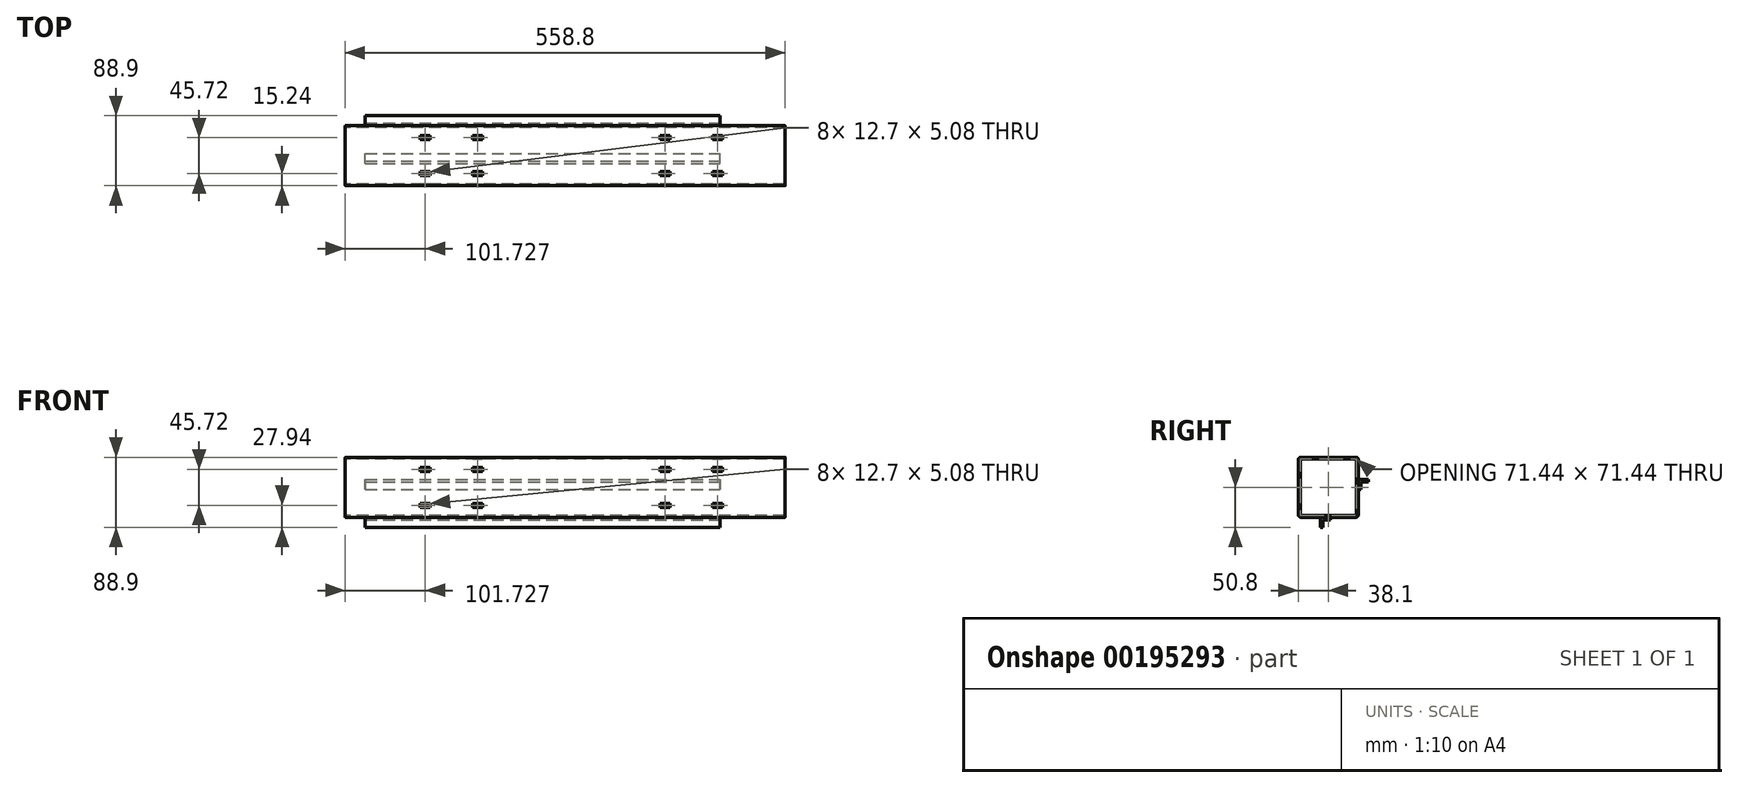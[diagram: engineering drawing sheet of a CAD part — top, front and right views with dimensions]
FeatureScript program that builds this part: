
annotation { "Feature Type Name" : "Feature", "Feature Type Description" : "" }
export const myFeature = defineFeature(function(context is Context, id is Id, definition is map)
    precondition{}
    {
        {
            var Q0;
            Q0=qCreatedBy(makeId("Right.planeOp"),FACE);
            var sketch = newSketch(context, id + "F0", { "sketchPlane" : qUnion([Q0])});
            skLineSegment(sketch, "E0.bottom", {"start": v(3.05, 0) * mm, "end": v(73.15, 0) * mm});
            skLineSegment(sketch, "E0.top", {"start": v(3.05, -76.2) * mm, "end": v(73.15, -76.2) * mm});
            skLineSegment(sketch, "E0.left", {"start": v(0, -3.05) * mm, "end": v(0, -73.15) * mm});
            skLineSegment(sketch, "E0.right", {"start": v(76.2, -3.05) * mm, "end": v(76.2, -73.15) * mm});
            skPoint(sketch, "E1.visualSharp", {"position": v(76.2, -76.2) * mm});
            skArc(sketch, "E1.filletArc", {"start": v(73.15, -76.2) * mm, "mid": v(75.3, -75.3) * mm, "end": v(76.2, -73.15) * mm});
            skPoint(sketch, "E2.visualSharp", {"position": v(76.2, 0) * mm});
            skArc(sketch, "E2.filletArc", {"start": v(76.2, -3.05) * mm, "mid": v(75.3, -0.9) * mm, "end": v(73.15, 0) * mm});
            skPoint(sketch, "E3.visualSharp", {"position": v(0, 0) * mm});
            skArc(sketch, "E3.filletArc", {"start": v(3.05, 0) * mm, "mid": v(0.9, -0.9) * mm, "end": v(0, -3.05) * mm});
            skPoint(sketch, "E4.visualSharp", {"position": v(0, -76.2) * mm});
            skArc(sketch, "E4.filletArc", {"start": v(0, -73.15) * mm, "mid": v(0.9, -75.3) * mm, "end": v(3.05, -76.2) * mm});
            skArc(sketch, "E5.0", {"start": v(73.82, -3.05) * mm, "mid": v(73.62, -2.58) * mm, "end": v(73.15, -2.38) * mm});
            skLineSegment(sketch, "E5.1", {"start": v(3.05, -2.38) * mm, "end": v(73.15, -2.38) * mm});
            skLineSegment(sketch, "E5.2", {"start": v(73.82, -3.05) * mm, "end": v(73.82, -73.15) * mm});
            skArc(sketch, "E5.3", {"start": v(3.05, -2.38) * mm, "mid": v(2.58, -2.58) * mm, "end": v(2.38, -3.05) * mm});
            skArc(sketch, "E5.4", {"start": v(73.15, -73.82) * mm, "mid": v(73.62, -73.62) * mm, "end": v(73.82, -73.15) * mm});
            skLineSegment(sketch, "E5.5", {"start": v(3.05, -73.82) * mm, "end": v(73.15, -73.82) * mm});
            skArc(sketch, "E5.6", {"start": v(2.38, -73.15) * mm, "mid": v(2.58, -73.62) * mm, "end": v(3.05, -73.82) * mm});
            skLineSegment(sketch, "E5.7", {"start": v(2.38, -3.05) * mm, "end": v(2.38, -73.15) * mm});
            skSolve(sketch);
        }
        {
            var Q0;
            Q0=makeQuery(id+"F0.imprint","IMPRINT",FACE,{"disambiguationData":[TD([[makeQuery(id+"F0.imprint","IMPRINT",EDGE,{"derivedFrom":sQuery(id+"F0.wireOp",EDGE,"E0.bottom")}),-1.0]])]});
            extrude(context, id + "F1", {"entities" : qUnion([Q0]), "depth" : 558.8 * mm});
        }
        {
            var Q0;
            Q0=makeQuery(id+"F1.opExtrude","SWEPT_FACE",FACE,{"disambiguationData":[OSD([sQuery(id+"F0.wireOp",EDGE,"E0.bottom")])]});
            var sketch = newSketch(context, id + "F2", { "sketchPlane" : qUnion([Q0])});
            skLineSegment(sketch, "E6", {"start": v(466.73, 76.2) * mm, "end": v(466.73, 0) * mm, "construction": true});
            skLineSegment(sketch, "E7", {"start": v(412.88, 76.2) * mm, "end": v(412.88, 0) * mm, "construction": true});
            skLineSegment(sketch, "E8.bottom", {"start": v(466.73, 63.5) * mm, "end": v(479.43, 63.5) * mm});
            skLineSegment(sketch, "E8.top", {"start": v(466.73, 58.42) * mm, "end": v(479.43, 58.42) * mm});
            skLineSegment(sketch, "E8.left", {"start": v(466.73, 63.5) * mm, "end": v(466.73, 58.42) * mm});
            skLineSegment(sketch, "E8.right", {"start": v(479.43, 63.5) * mm, "end": v(479.43, 58.42) * mm});
            skLineSegment(sketch, "E9.bottom", {"start": v(466.73, 17.78) * mm, "end": v(479.43, 17.78) * mm});
            skLineSegment(sketch, "E9.top", {"start": v(466.73, 12.7) * mm, "end": v(479.43, 12.7) * mm});
            skLineSegment(sketch, "E9.left", {"start": v(466.73, 17.78) * mm, "end": v(466.73, 12.7) * mm});
            skLineSegment(sketch, "E9.right", {"start": v(479.43, 17.78) * mm, "end": v(479.43, 12.7) * mm});
            skLineSegment(sketch, "E10.bottom", {"start": v(412.88, 58.42) * mm, "end": v(400.18, 58.42) * mm});
            skLineSegment(sketch, "E10.top", {"start": v(412.88, 63.5) * mm, "end": v(400.18, 63.5) * mm});
            skLineSegment(sketch, "E10.left", {"start": v(412.88, 58.42) * mm, "end": v(412.88, 63.5) * mm});
            skLineSegment(sketch, "E10.right", {"start": v(400.18, 58.42) * mm, "end": v(400.18, 63.5) * mm});
            skLineSegment(sketch, "E11.bottom", {"start": v(412.88, 17.78) * mm, "end": v(400.18, 17.78) * mm});
            skLineSegment(sketch, "E11.top", {"start": v(412.88, 12.7) * mm, "end": v(400.18, 12.7) * mm});
            skLineSegment(sketch, "E11.left", {"start": v(412.88, 17.78) * mm, "end": v(412.88, 12.7) * mm});
            skLineSegment(sketch, "E11.right", {"start": v(400.18, 17.78) * mm, "end": v(400.18, 12.7) * mm});
            skPoint(sketch, "E12", {"position": v(466.73, 38.1) * mm});
            skPoint(sketch, "E13", {"position": v(412.88, 38.1) * mm});
            skLineSegment(sketch, "E14", {"start": v(161.93, 73.15) * mm, "end": v(161.93, 3.05) * mm, "construction": true});
            skLineSegment(sketch, "E15.bottom", {"start": v(161.93, 63.5) * mm, "end": v(174.63, 63.5) * mm});
            skLineSegment(sketch, "E15.top", {"start": v(161.93, 58.42) * mm, "end": v(174.63, 58.42) * mm});
            skLineSegment(sketch, "E15.left", {"start": v(161.93, 63.5) * mm, "end": v(161.93, 58.42) * mm});
            skLineSegment(sketch, "E15.right", {"start": v(174.63, 63.5) * mm, "end": v(174.63, 58.42) * mm});
            skLineSegment(sketch, "E16.bottom", {"start": v(161.93, 17.78) * mm, "end": v(174.63, 17.78) * mm});
            skLineSegment(sketch, "E16.top", {"start": v(161.93, 12.7) * mm, "end": v(174.63, 12.7) * mm});
            skLineSegment(sketch, "E16.left", {"start": v(161.93, 17.78) * mm, "end": v(161.93, 12.7) * mm});
            skLineSegment(sketch, "E16.right", {"start": v(174.63, 17.78) * mm, "end": v(174.63, 12.7) * mm});
            skLineSegment(sketch, "E17.bottom", {"start": v(108.08, 58.42) * mm, "end": v(95.38, 58.42) * mm});
            skLineSegment(sketch, "E17.top", {"start": v(108.08, 63.5) * mm, "end": v(95.38, 63.5) * mm});
            skLineSegment(sketch, "E17.left", {"start": v(108.08, 58.42) * mm, "end": v(108.08, 63.5) * mm});
            skLineSegment(sketch, "E17.right", {"start": v(95.38, 58.42) * mm, "end": v(95.38, 63.5) * mm});
            skLineSegment(sketch, "E18.bottom", {"start": v(108.08, 17.78) * mm, "end": v(95.38, 17.78) * mm});
            skLineSegment(sketch, "E18.top", {"start": v(108.08, 12.7) * mm, "end": v(95.38, 12.7) * mm});
            skLineSegment(sketch, "E18.left", {"start": v(108.08, 17.78) * mm, "end": v(108.08, 12.7) * mm});
            skLineSegment(sketch, "E18.right", {"start": v(95.38, 17.78) * mm, "end": v(95.38, 12.7) * mm});
            skPoint(sketch, "E19", {"position": v(161.93, 38.1) * mm});
            skPoint(sketch, "E20", {"position": v(108.08, 38.1) * mm});
            skLineSegment(sketch, "E21", {"start": v(108.08, 73.15) * mm, "end": v(108.08, 3.05) * mm, "construction": true});
            skPoint(sketch, "E22", {"position": v(406.53, 38.1) * mm});
            skPoint(sketch, "E22.positionSnap0", {"position": v(406.53, 58.42) * mm});
            skPoint(sketch, "E23", {"position": v(473.08, 38.1) * mm});
            skPoint(sketch, "E23.positionSnap0", {"position": v(473.08, 58.42) * mm});
            skPoint(sketch, "E24", {"position": v(168.28, 38.1) * mm});
            skPoint(sketch, "E24.positionSnap0", {"position": v(168.28, 58.42) * mm});
            skPoint(sketch, "E25", {"position": v(101.73, 38.1) * mm});
            skPoint(sketch, "E25.positionSnap0", {"position": v(101.73, 58.42) * mm});
            skSolve(sketch);
        }
        {
            var Q0;
            Q0=makeQuery(id+"F2.imprint","IMPRINT",FACE,{"disambiguationData":[TD([[makeQuery(id+"F2.imprint","IMPRINT",EDGE,{"derivedFrom":sQuery(id+"F2.wireOp",EDGE,"E8.bottom")}),-1.0]])]});
            var Q1;
            Q1=makeQuery(id+"F2.imprint","IMPRINT",FACE,{"disambiguationData":[TD([[makeQuery(id+"F2.imprint","IMPRINT",EDGE,{"derivedFrom":sQuery(id+"F2.wireOp",EDGE,"E9.bottom")}),-1.0]])]});
            var Q2;
            Q2=makeQuery(id+"F2.imprint","IMPRINT",FACE,{"disambiguationData":[TD([[makeQuery(id+"F2.imprint","IMPRINT",EDGE,{"derivedFrom":sQuery(id+"F2.wireOp",EDGE,"E11.bottom")}),1.0]])]});
            var Q3;
            Q3=makeQuery(id+"F2.imprint","IMPRINT",FACE,{"disambiguationData":[TD([[makeQuery(id+"F2.imprint","IMPRINT",EDGE,{"derivedFrom":sQuery(id+"F2.wireOp",EDGE,"E10.bottom")}),-1.0]])]});
            extrude(context, id + "F3", {"entities" : qUnion([Q0, Q1, Q2, Q3]), "operationType" : NewBodyOperationType.REMOVE, "oppositeDirection" : true, "depth" : 2.38 * mm});
        }
        {
            var Q0;
            Q0=makeQuery(id+"F2.imprint","IMPRINT",FACE,{"disambiguationData":[TD([[makeQuery(id+"F2.imprint","IMPRINT",EDGE,{"derivedFrom":sQuery(id+"F2.wireOp",EDGE,"E15.bottom")}),-1.0]])]});
            var Q1;
            Q1=makeQuery(id+"F2.imprint","IMPRINT",FACE,{"disambiguationData":[TD([[makeQuery(id+"F2.imprint","IMPRINT",EDGE,{"derivedFrom":sQuery(id+"F2.wireOp",EDGE,"E16.bottom")}),-1.0]])]});
            var Q2;
            Q2=makeQuery(id+"F2.imprint","IMPRINT",FACE,{"disambiguationData":[TD([[makeQuery(id+"F2.imprint","IMPRINT",EDGE,{"derivedFrom":sQuery(id+"F2.wireOp",EDGE,"E18.bottom")}),1.0]])]});
            var Q3;
            Q3=makeQuery(id+"F2.imprint","IMPRINT",FACE,{"disambiguationData":[TD([[makeQuery(id+"F2.imprint","IMPRINT",EDGE,{"derivedFrom":sQuery(id+"F2.wireOp",EDGE,"E17.bottom")}),-1.0]])]});
            extrude(context, id + "F4", {"entities" : qUnion([Q0, Q1, Q2, Q3]), "operationType" : NewBodyOperationType.REMOVE, "oppositeDirection" : true, "depth" : 2.38 * mm});
        }
        {
            var Q0;
            Q0=makeQuery(id+"F1.opExtrude","SWEPT_FACE",FACE,{"disambiguationData":[OSD([sQuery(id+"F0.wireOp",EDGE,"E0.left")])]});
            var sketch = newSketch(context, id + "F5", { "sketchPlane" : qUnion([Q0])});
            skLineSegment(sketch, "E26", {"start": v(466.73, -3.05) * mm, "end": v(466.73, -73.15) * mm, "construction": true});
            skLineSegment(sketch, "E27", {"start": v(412.88, -3.05) * mm, "end": v(412.88, -73.15) * mm, "construction": true});
            skLineSegment(sketch, "E28", {"start": v(161.93, -3.05) * mm, "end": v(161.93, -73.15) * mm, "construction": true});
            skPoint(sketch, "E28.endSnap0", {"position": v(279.4, -73.15) * mm});
            skLineSegment(sketch, "E29", {"start": v(108.08, -3.05) * mm, "end": v(108.08, -73.15) * mm, "construction": true});
            skPoint(sketch, "E30", {"position": v(466.73, -38.1) * mm});
            skPoint(sketch, "E31", {"position": v(412.88, -38.1) * mm});
            skPoint(sketch, "E32", {"position": v(161.93, -38.1) * mm});
            skPoint(sketch, "E33", {"position": v(108.08, -38.1) * mm});
            skLineSegment(sketch, "E34.bottom", {"start": v(466.73, -12.7) * mm, "end": v(479.43, -12.7) * mm});
            skLineSegment(sketch, "E34.top", {"start": v(466.73, -17.78) * mm, "end": v(479.43, -17.78) * mm});
            skLineSegment(sketch, "E34.left", {"start": v(466.73, -12.7) * mm, "end": v(466.73, -17.78) * mm});
            skLineSegment(sketch, "E34.right", {"start": v(479.43, -12.7) * mm, "end": v(479.43, -17.78) * mm});
            skLineSegment(sketch, "E35.bottom", {"start": v(466.73, -58.42) * mm, "end": v(479.43, -58.42) * mm});
            skLineSegment(sketch, "E35.top", {"start": v(466.73, -63.5) * mm, "end": v(479.43, -63.5) * mm});
            skLineSegment(sketch, "E35.left", {"start": v(466.73, -58.42) * mm, "end": v(466.73, -63.5) * mm});
            skLineSegment(sketch, "E35.right", {"start": v(479.43, -58.42) * mm, "end": v(479.43, -63.5) * mm});
            skLineSegment(sketch, "E36.left", {"start": v(412.88, -58.42) * mm, "end": v(412.88, -63.5) * mm});
            skLineSegment(sketch, "E37.left", {"start": v(412.88, -12.7) * mm, "end": v(412.88, -17.78) * mm});
            skLineSegment(sketch, "E38.bottom", {"start": v(161.93, -12.7) * mm, "end": v(174.63, -12.7) * mm});
            skLineSegment(sketch, "E38.top", {"start": v(161.93, -17.78) * mm, "end": v(174.63, -17.78) * mm});
            skLineSegment(sketch, "E38.left", {"start": v(161.93, -12.7) * mm, "end": v(161.93, -17.78) * mm});
            skLineSegment(sketch, "E38.right", {"start": v(174.63, -12.7) * mm, "end": v(174.63, -17.78) * mm});
            skLineSegment(sketch, "E39.bottom", {"start": v(161.93, -58.42) * mm, "end": v(174.63, -58.42) * mm});
            skLineSegment(sketch, "E39.top", {"start": v(161.93, -63.5) * mm, "end": v(174.63, -63.5) * mm});
            skLineSegment(sketch, "E39.left", {"start": v(161.93, -58.42) * mm, "end": v(161.93, -63.5) * mm});
            skLineSegment(sketch, "E39.right", {"start": v(174.63, -58.42) * mm, "end": v(174.63, -63.5) * mm});
            skLineSegment(sketch, "E40.bottom", {"start": v(108.08, -63.5) * mm, "end": v(95.38, -63.5) * mm});
            skLineSegment(sketch, "E40.top", {"start": v(108.08, -58.42) * mm, "end": v(95.38, -58.42) * mm});
            skLineSegment(sketch, "E40.left", {"start": v(108.08, -63.5) * mm, "end": v(108.08, -58.42) * mm});
            skLineSegment(sketch, "E40.right", {"start": v(95.38, -63.5) * mm, "end": v(95.38, -58.42) * mm});
            skLineSegment(sketch, "E41.bottom", {"start": v(108.08, -17.78) * mm, "end": v(95.38, -17.78) * mm});
            skLineSegment(sketch, "E41.top", {"start": v(108.08, -12.7) * mm, "end": v(95.38, -12.7) * mm});
            skLineSegment(sketch, "E41.left", {"start": v(108.08, -17.78) * mm, "end": v(108.08, -12.7) * mm});
            skLineSegment(sketch, "E41.right", {"start": v(95.38, -17.78) * mm, "end": v(95.38, -12.7) * mm});
            skLineSegment(sketch, "E42.bottom", {"start": v(412.88, -12.7) * mm, "end": v(400.18, -12.7) * mm});
            skLineSegment(sketch, "E42.top", {"start": v(412.88, -17.78) * mm, "end": v(400.18, -17.78) * mm});
            skLineSegment(sketch, "E42.right", {"start": v(400.18, -12.7) * mm, "end": v(400.18, -17.78) * mm});
            skLineSegment(sketch, "E43.bottom", {"start": v(412.88, -58.42) * mm, "end": v(400.18, -58.42) * mm});
            skLineSegment(sketch, "E43.top", {"start": v(412.88, -63.5) * mm, "end": v(400.18, -63.5) * mm});
            skLineSegment(sketch, "E43.right", {"start": v(400.18, -58.42) * mm, "end": v(400.18, -63.5) * mm});
            skPoint(sketch, "E44", {"position": v(168.28, -38.1) * mm});
            skPoint(sketch, "E44.positionSnap0", {"position": v(168.28, -17.78) * mm});
            skPoint(sketch, "E45", {"position": v(101.73, -38.1) * mm});
            skPoint(sketch, "E45.positionSnap0", {"position": v(101.73, -17.78) * mm});
            skPoint(sketch, "E46", {"position": v(406.53, -38.1) * mm});
            skPoint(sketch, "E46.positionSnap0", {"position": v(406.53, -17.78) * mm});
            skPoint(sketch, "E47", {"position": v(473.08, -38.1) * mm});
            skPoint(sketch, "E47.positionSnap0", {"position": v(473.08, -17.78) * mm});
            skLineSegment(sketch, "E48", {"start": v(473.08, -17.78) * mm, "end": v(473.08, -58.42) * mm, "construction": true});
            skSolve(sketch);
        }
        {
            var Q0;
            Q0=makeQuery(id+"F5.imprint","IMPRINT",FACE,{"disambiguationData":[TD([[makeQuery(id+"F5.imprint","IMPRINT",EDGE,{"derivedFrom":sQuery(id+"F5.wireOp",EDGE,"E34.bottom")}),-1.0]])]});
            var Q1;
            Q1=makeQuery(id+"F5.imprint","IMPRINT",FACE,{"disambiguationData":[TD([[makeQuery(id+"F5.imprint","IMPRINT",EDGE,{"derivedFrom":sQuery(id+"F5.wireOp",EDGE,"E35.bottom")}),-1.0]])]});
            var Q2;
            Q2=makeQuery(id+"F5.imprint","IMPRINT",FACE,{"disambiguationData":[TD([[makeQuery(id+"F5.imprint","IMPRINT",EDGE,{"derivedFrom":sQuery(id+"F5.wireOp",EDGE,"E43.bottom")}),1.0]])]});
            var Q3;
            Q3=makeQuery(id+"F5.imprint","IMPRINT",FACE,{"disambiguationData":[TD([[makeQuery(id+"F5.imprint","IMPRINT",EDGE,{"derivedFrom":sQuery(id+"F5.wireOp",EDGE,"E42.bottom")}),1.0]])]});
            var Q4;
            Q4=makeQuery(id+"F5.imprint","IMPRINT",FACE,{"disambiguationData":[TD([[makeQuery(id+"F5.imprint","IMPRINT",EDGE,{"derivedFrom":sQuery(id+"F5.wireOp",EDGE,"E39.bottom")}),-1.0]])]});
            var Q5;
            Q5=makeQuery(id+"F5.imprint","IMPRINT",FACE,{"disambiguationData":[TD([[makeQuery(id+"F5.imprint","IMPRINT",EDGE,{"derivedFrom":sQuery(id+"F5.wireOp",EDGE,"E38.bottom")}),-1.0]])]});
            var Q6;
            Q6=makeQuery(id+"F5.imprint","IMPRINT",FACE,{"disambiguationData":[TD([[makeQuery(id+"F5.imprint","IMPRINT",EDGE,{"derivedFrom":sQuery(id+"F5.wireOp",EDGE,"E40.bottom")}),-1.0]])]});
            var Q7;
            Q7=makeQuery(id+"F5.imprint","IMPRINT",FACE,{"disambiguationData":[TD([[makeQuery(id+"F5.imprint","IMPRINT",EDGE,{"derivedFrom":sQuery(id+"F5.wireOp",EDGE,"E41.bottom")}),-1.0]])]});
            extrude(context, id + "F6", {"entities" : qUnion([Q0, Q1, Q2, Q3, Q4, Q5, Q6, Q7]), "operationType" : NewBodyOperationType.REMOVE, "oppositeDirection" : true, "depth" : 2.38 * mm});
        }
        {
            var Q0;
            Q0=makeQuery(id+"F1.opExtrude","CAP_FACE",FACE,{"disambiguationData":[OSD([sQuery(id+"F0.wireOp",EDGE,"E0.bottom"),sQuery(id+"F0.wireOp",EDGE,"E0.top"),sQuery(id+"F0.wireOp",EDGE,"E0.left"),sQuery(id+"F0.wireOp",EDGE,"E0.right"),sQuery(id+"F0.wireOp",EDGE,"E1.filletArc"),sQuery(id+"F0.wireOp",EDGE,"E2.filletArc"),sQuery(id+"F0.wireOp",EDGE,"E3.filletArc"),sQuery(id+"F0.wireOp",EDGE,"E4.filletArc"),sQuery(id+"F0.wireOp",EDGE,"E5.0"),sQuery(id+"F0.wireOp",EDGE,"E5.1"),sQuery(id+"F0.wireOp",EDGE,"E5.2"),sQuery(id+"F0.wireOp",EDGE,"E5.3"),sQuery(id+"F0.wireOp",EDGE,"E5.4"),sQuery(id+"F0.wireOp",EDGE,"E5.5"),sQuery(id+"F0.wireOp",EDGE,"E5.6"),sQuery(id+"F0.wireOp",EDGE,"E5.7")])],"isStart":false});
            var sketch = newSketch(context, id + "F7", { "sketchPlane" : qUnion([Q0])});
            skLineSegment(sketch, "E49", {"start": v(76.2, -27.94) * mm, "end": v(76.2, -40.64) * mm});
            skLineSegment(sketch, "E50", {"start": v(76.2, -40.64) * mm, "end": v(79.38, -40.64) * mm});
            skLineSegment(sketch, "E51", {"start": v(79.38, -40.64) * mm, "end": v(79.38, -31.12) * mm});
            skLineSegment(sketch, "E52", {"start": v(79.38, -31.12) * mm, "end": v(88.9, -31.12) * mm});
            skLineSegment(sketch, "E53", {"start": v(88.9, -31.12) * mm, "end": v(88.9, -27.94) * mm});
            skLineSegment(sketch, "E54", {"start": v(88.9, -27.94) * mm, "end": v(76.2, -27.94) * mm});
            skLineSegment(sketch, "E55", {"start": v(27.94, -76.2) * mm, "end": v(27.94, -88.9) * mm});
            skLineSegment(sketch, "E56", {"start": v(27.94, -88.9) * mm, "end": v(31.12, -88.9) * mm});
            skLineSegment(sketch, "E57", {"start": v(31.12, -88.9) * mm, "end": v(31.12, -79.37) * mm});
            skLineSegment(sketch, "E58", {"start": v(31.12, -79.37) * mm, "end": v(40.64, -79.37) * mm});
            skLineSegment(sketch, "E59", {"start": v(40.64, -79.37) * mm, "end": v(40.64, -76.2) * mm});
            skLineSegment(sketch, "E60", {"start": v(40.64, -76.2) * mm, "end": v(27.94, -76.2) * mm});
            skSolve(sketch);
        }
        {
            var Q0;
            Q0=makeQuery(id+"F7.imprint","IMPRINT",FACE,{"disambiguationData":[TD([[makeQuery(id+"F7.imprint","IMPRINT",EDGE,{"derivedFrom":sQuery(id+"F7.wireOp",EDGE,"E49")}),1.0]])]});
            var Q1;
            Q1=makeQuery(id+"F7.imprint","IMPRINT",FACE,{"disambiguationData":[TD([[makeQuery(id+"F7.imprint","IMPRINT",EDGE,{"derivedFrom":sQuery(id+"F7.wireOp",EDGE,"E55")}),1.0]])]});
            extrude(context, id + "F8", {"entities" : qUnion([Q0, Q1]), "operationType" : NewBodyOperationType.ADD, "oppositeDirection" : true, "depth" : 533.4 * mm});
        }
        {
            var Q0;
            Q0=makeQuery(id+"F7.imprint","IMPRINT",FACE,{"disambiguationData":[TD([[makeQuery(id+"F7.imprint","IMPRINT",EDGE,{"derivedFrom":sQuery(id+"F7.wireOp",EDGE,"E49")}),1.0]])]});
            var Q1;
            Q1=makeQuery(id+"F7.imprint","IMPRINT",FACE,{"disambiguationData":[TD([[makeQuery(id+"F7.imprint","IMPRINT",EDGE,{"derivedFrom":sQuery(id+"F7.wireOp",EDGE,"E55")}),1.0]])]});
            extrude(context, id + "F9", {"entities" : qUnion([Q0, Q1]), "operationType" : NewBodyOperationType.REMOVE, "oppositeDirection" : true, "depth" : 82.55 * mm});
        }
    });
